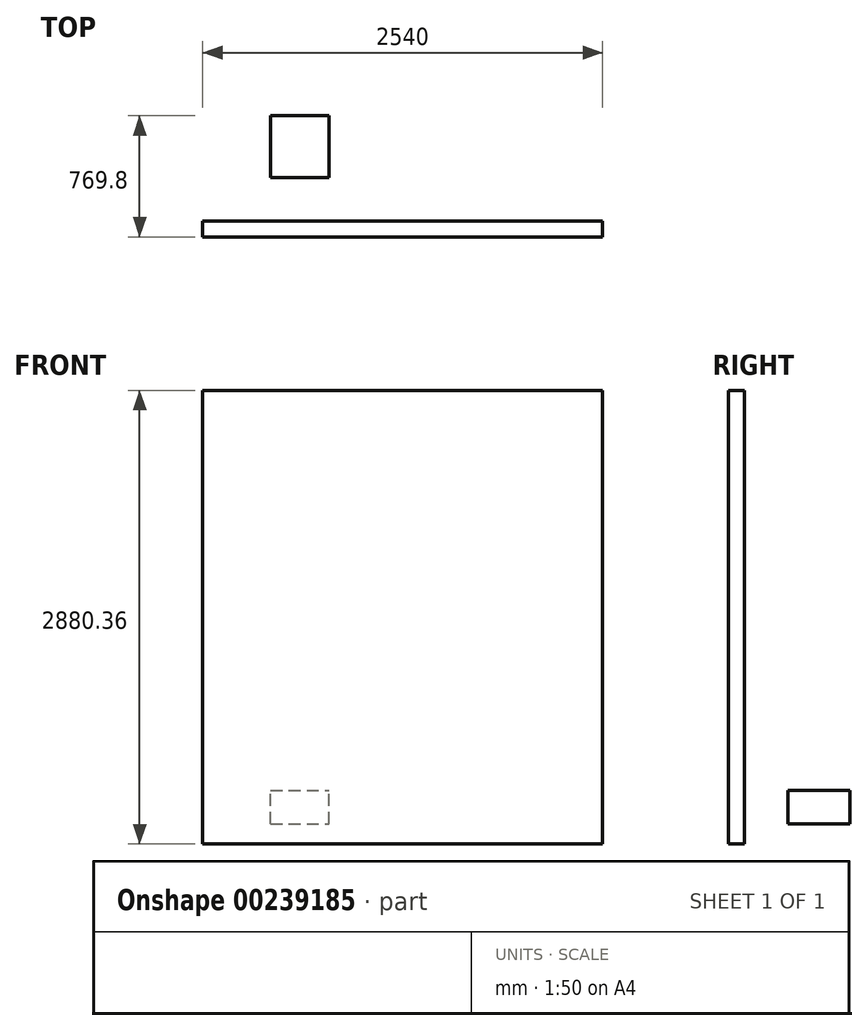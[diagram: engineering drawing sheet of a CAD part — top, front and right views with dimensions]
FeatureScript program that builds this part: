
annotation { "Feature Type Name" : "Feature", "Feature Type Description" : "" }
export const myFeature = defineFeature(function(context is Context, id is Id, definition is map)
    precondition{}
    {
        {
            assignVariable(context, id + "F0", {"name" : "l", "anyValue" : 100});
        }
        {
            var Q0;
            Q0=qCreatedBy(makeId("Front.planeOp"),FACE);
            var sketch = newSketch(context, id + "F1", { "sketchPlane" : qUnion([Q0])});
            skLineSegment(sketch, "E0.bottom", {"start": v(1270, 1270) * mm, "end": v(-1270, 1270) * mm});
            skLineSegment(sketch, "E0.top", {"start": v(1270, -1270) * mm, "end": v(-1270, -1270) * mm});
            skLineSegment(sketch, "E0.left", {"start": v(1270, 1270) * mm, "end": v(1270, -1270) * mm});
            skLineSegment(sketch, "E0.right", {"start": v(-1270, 1270) * mm, "end": v(-1270, -1270) * mm});
            skPoint(sketch, "E0.middle", {"position": v(0, 0) * mm});
            skSolve(sketch);
        }
        {
            var Q0;
            Q0=makeQuery(id+"F1.imprint","IMPRINT",FACE,{"disambiguationData":[TD([[makeQuery(id+"F1.imprint","IMPRINT",EDGE,{"derivedFrom":sQuery(id+"F1.wireOp",EDGE,"E0.bottom")}),1.0]])]});
            extrude(context, id + "F2", {"entities" : qUnion([Q0]), "endBound" : BoundingType.SYMMETRIC, "depth" : (getVariable(context, 'l')) * mm});
        }
        {
            var Q0;
            Q0=makeQuery(id+"F2.opExtrude","SWEPT_FACE",FACE,{"disambiguationData":[OSD([sQuery(id+"F1.wireOp",EDGE,"E0.bottom")])]});
            var sketch = newSketch(context, id + "F3", { "sketchPlane" : qUnion([Q0])});
            skLineSegment(sketch, "E1.bottom", {"start": v(-838.95, 719.8) * mm, "end": v(-466.8, 719.8) * mm});
            skLineSegment(sketch, "E1.top", {"start": v(-838.95, 328.07) * mm, "end": v(-466.8, 328.07) * mm});
            skLineSegment(sketch, "E1.left", {"start": v(-838.95, 719.8) * mm, "end": v(-838.95, 328.07) * mm});
            skLineSegment(sketch, "E1.right", {"start": v(-466.8, 719.8) * mm, "end": v(-466.8, 328.07) * mm});
            skSolve(sketch);
        }
        {
            var Q0;
            Q0=makeQuery(id+"F3.imprint","IMPRINT",FACE,{"disambiguationData":[TD([[makeQuery(id+"F3.imprint","IMPRINT",EDGE,{"derivedFrom":sQuery(id+"F3.wireOp",EDGE,"E1.bottom")}),-1.0]])]});
            extrude(context, id + "F4", {"entities" : qUnion([Q0]), "operationType" : NewBodyOperationType.REMOVE, "oppositeDirection" : true, "depth" : 127 * mm});
        }
        {
            var Q0;
            Q0=makeQuery(id+"F2.opExtrude","SWEPT_FACE",FACE,{"disambiguationData":[OSD([sQuery(id+"F1.wireOp",EDGE,"E0.top")])]});
            var sketch = newSketch(context, id + "F5", { "sketchPlane" : qUnion([Q0])});
            skLineSegment(sketch, "E2.0", {"start": v(-838.95, -328.07) * mm, "end": v(-466.8, -328.07) * mm});
            skLineSegment(sketch, "E3.0", {"start": v(-466.8, -719.8) * mm, "end": v(-466.8, -328.07) * mm});
            skLineSegment(sketch, "E4.0", {"start": v(-838.95, -719.8) * mm, "end": v(-466.8, -719.8) * mm});
            skPoint(sketch, "E5.0", {"position": v(-838.95, -523.93) * mm});
            skLineSegment(sketch, "E6.0", {"start": v(-838.95, -719.8) * mm, "end": v(-838.95, -328.07) * mm});
            skSolve(sketch);
        }
        {
            var Q0;
            {var subQ0=sQuery(id+"F1.wireOp",EDGE,"E0.top");Q0=makeQuery(id+"F5.imprint","IMPRINT",FACE,{"disambiguationData":[TD([[makeQuery(id+"F5.imprint","IMPRINT",EDGE,{"derivedFrom":makeQuery(id+"F2.opExtrude","CAP_EDGE",EDGE,{"disambiguationData":[OSD([subQ0])],"isStart":true})}),-1.0]])]});}
            var Q1;
            Q1=makeQuery(id+"F5.imprint","IMPRINT",FACE,{"disambiguationData":[TD([[makeQuery(id+"F5.imprint","IMPRINT",EDGE,{"derivedFrom":sQuery(id+"F5.wireOp",EDGE,"E2.0")}),-1.0]])]});
            extrude(context, id + "F6", {"entities" : qUnion([Q0, Q1]), "operationType" : NewBodyOperationType.ADD, "depth" : 127 * mm});
        }
        {
            var Q0;
            Q0=makeQuery(id+"F5.imprint","IMPRINT",FACE,{"disambiguationData":[TD([[makeQuery(id+"F5.imprint","IMPRINT",EDGE,{"derivedFrom":sQuery(id+"F5.wireOp",EDGE,"E2.0")}),-1.0]])]});
            extrude(context, id + "F7", {"entities" : qUnion([Q0]), "operationType" : NewBodyOperationType.ADD, "depth" : 127 * mm});
        }
        {
            var Q0;
            Q0 = qSketchRegion(id + "F5", true);
            extrude(context, id + "F8", {"entities" : qUnion([Q0]), "operationType" : NewBodyOperationType.ADD, "depth" : 127 * mm});
        }
        {
            var Q0;
            Q0 = qSketchRegion(id + "F5", true);
            var Q1;
            Q1=makeQuery(id+"F6.opExtrude","CAP_FACE",FACE,{"disambiguationData":[OSD([sQuery(id+"F1.wireOp",EDGE,"E0.top"),sQuery(id+"F1.wireOp",EDGE,"E0.left"),sQuery(id+"F1.wireOp",EDGE,"E0.right")])],"isStart":false});
            extrude(context, id + "F9", {"entities" : qUnion([Q0, Q1]), "operationType" : NewBodyOperationType.ADD, "depth" : 213.36 * mm});
        }
    });
